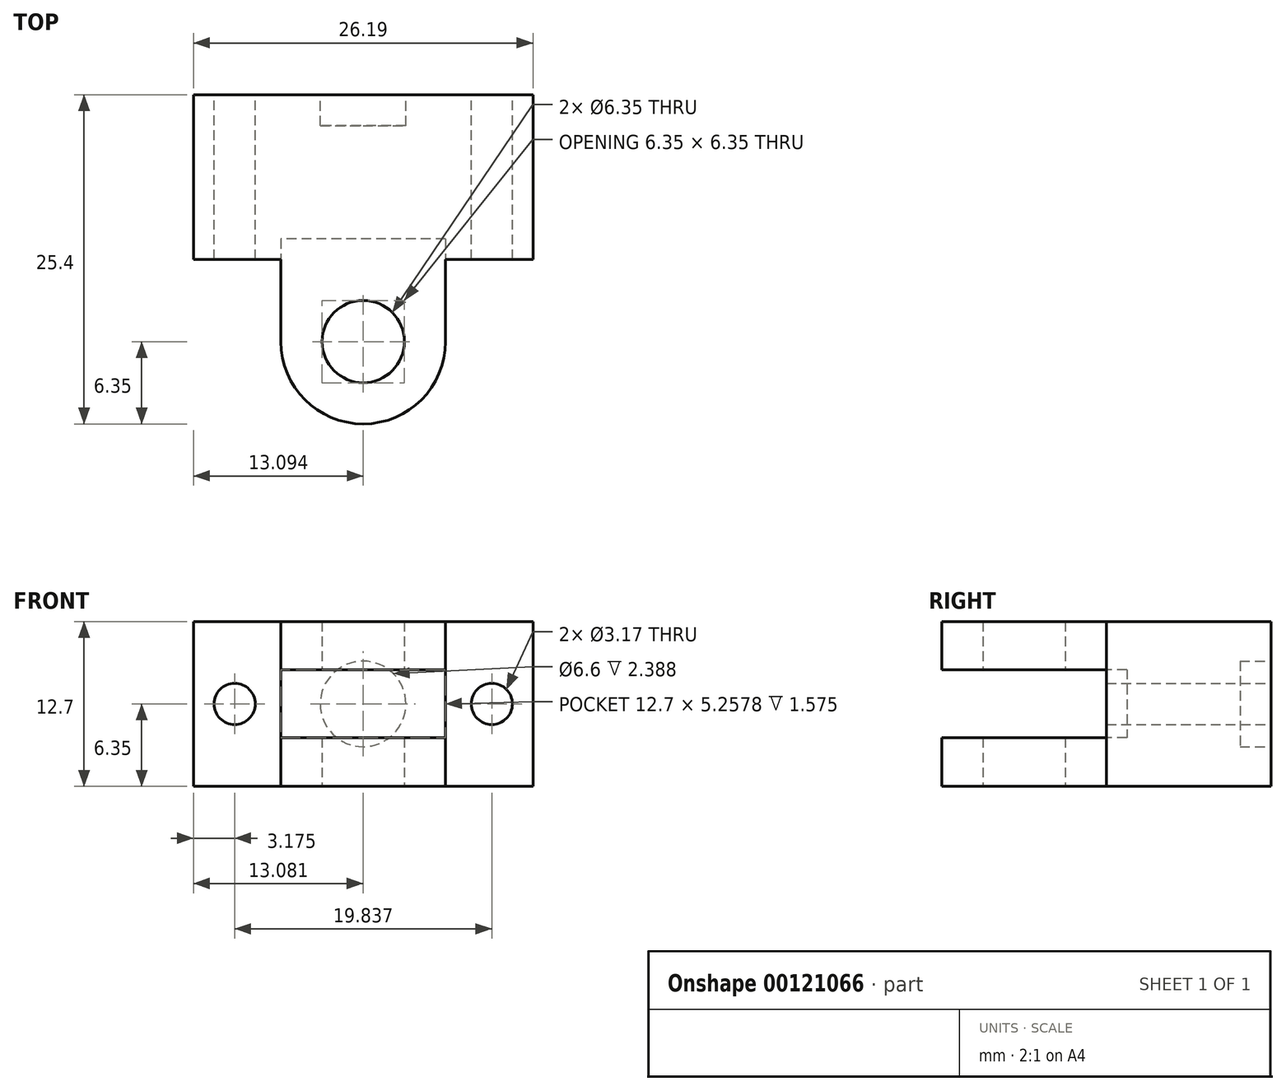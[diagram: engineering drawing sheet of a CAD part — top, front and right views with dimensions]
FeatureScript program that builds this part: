
annotation { "Feature Type Name" : "Feature", "Feature Type Description" : "" }
export const myFeature = defineFeature(function(context is Context, id is Id, definition is map)
    precondition{}
    {
        {
            var Q0;
            Q0=qCreatedBy(makeId("Top.planeOp"),FACE);
            var sketch = newSketch(context, id + "F0", { "sketchPlane" : qUnion([Q0])});
            skLineSegment(sketch, "E0.bottom", {"start": v(0, 0) * mm, "end": v(26.19, 0) * mm});
            skLineSegment(sketch, "E0.top", {"start": v(0, -12.7) * mm, "end": v(6.74, -12.7) * mm});
            skLineSegment(sketch, "E0.left", {"start": v(0, 0) * mm, "end": v(0, -12.7) * mm});
            skLineSegment(sketch, "E0.right", {"start": v(26.19, 0) * mm, "end": v(26.19, -12.7) * mm});
            skArc(sketch, "E1", {"start": v(6.74, -19.05) * mm, "mid": v(13.1, -25.4) * mm, "end": v(19.44, -19.05) * mm});
            skPoint(sketch, "E1.centerSnap0", {"position": v(13.1, -12.7) * mm});
            skLineSegment(sketch, "E2", {"start": v(6.74, -19.05) * mm, "end": v(6.74, -12.7) * mm});
            skLineSegment(sketch, "E3", {"start": v(19.44, -19.05) * mm, "end": v(19.44, -12.7) * mm});
            skLineSegment(sketch, "E4.trimOffspring", {"start": v(19.44, -12.7) * mm, "end": v(26.19, -12.7) * mm});
            skCircle(sketch, "E5", {"center": v(13.1, -19.05) * mm, "radius": 3.18 * mm});
            skSolve(sketch);
        }
        {
            var Q0;
            Q0=makeQuery(id+"F0.imprint","IMPRINT",FACE,{"disambiguationData":[TD([[makeQuery(id+"F0.imprint","IMPRINT",EDGE,{"derivedFrom":sQuery(id+"F0.wireOp",EDGE,"E0.bottom")}),-1.0]])]});
            extrude(context, id + "F1", {"entities" : qUnion([Q0]), "depth" : 12.7 * mm});
        }
        {
            var Q0;
            Q0=makeQuery(id+"F1.opExtrude","SWEPT_FACE",FACE,{"disambiguationData":[OSD([sQuery(id+"F0.wireOp",EDGE,"E0.bottom")])]});
            var sketch = newSketch(context, id + "F2", { "sketchPlane" : qUnion([Q0])});
            skCircle(sketch, "E6", {"center": v(-3.18, 6.35) * mm, "radius": 1.59 * mm});
            skCircle(sketch, "E7", {"center": v(-23.01, 6.35) * mm, "radius": 1.59 * mm});
            skSolve(sketch);
        }
        {
            var Q0;
            Q0 = qSketchRegion(id + "F2", true);
            extrude(context, id + "F3", {"entities" : qUnion([Q0]), "operationType" : NewBodyOperationType.REMOVE, "endBound" : BoundingType.THROUGH_ALL, "oppositeDirection" : true, "depth" : 25.4 * mm});
        }
        {
            var Q0;
            Q0=makeQuery(id+"F1.opExtrude","SWEPT_FACE",FACE,{"disambiguationData":[OSD([sQuery(id+"F0.wireOp",EDGE,"E0.bottom")])]});
            var sketch = newSketch(context, id + "F4", { "sketchPlane" : qUnion([Q0])});
            skCircle(sketch, "E8", {"center": v(-13.08, 6.35) * mm, "radius": 3.3 * mm});
            skSolve(sketch);
        }
        {
            var Q0;
            Q0 = qSketchRegion(id + "F4", true);
            extrude(context, id + "F5", {"entities" : qUnion([Q0]), "operationType" : NewBodyOperationType.REMOVE, "oppositeDirection" : true, "depth" : 2.4 * mm});
        }
        {
            var Q0;
            Q0=makeQuery(id+"F1.opExtrude","SWEPT_FACE",FACE,{"disambiguationData":[OSD([sQuery(id+"F0.wireOp",EDGE,"E4.trimOffspring")])]});
            var sketch = newSketch(context, id + "F6", { "sketchPlane" : qUnion([Q0])});
            skLineSegment(sketch, "E9.bottom", {"start": v(19.44, 9) * mm, "end": v(6.74, 9) * mm});
            skLineSegment(sketch, "E9.top", {"start": v(19.44, 3.73) * mm, "end": v(6.74, 3.73) * mm});
            skLineSegment(sketch, "E9.left", {"start": v(19.44, 9) * mm, "end": v(19.44, 3.73) * mm});
            skLineSegment(sketch, "E9.right", {"start": v(6.74, 9) * mm, "end": v(6.74, 3.73) * mm});
            skSolve(sketch);
        }
        {
            var Q0;
            Q0 = qSketchRegion(id + "F6", true);
            extrude(context, id + "F7", {"entities" : qUnion([Q0]), "operationType" : NewBodyOperationType.REMOVE, "endBound" : BoundingType.THROUGH_ALL, "depth" : 25.4 * mm});
        }
        {
            var Q0;
            Q0 = qSketchRegion(id + "F6", true);
            extrude(context, id + "F8", {"entities" : qUnion([Q0]), "operationType" : NewBodyOperationType.REMOVE, "oppositeDirection" : true, "depth" : 1.57 * mm});
        }
    });
